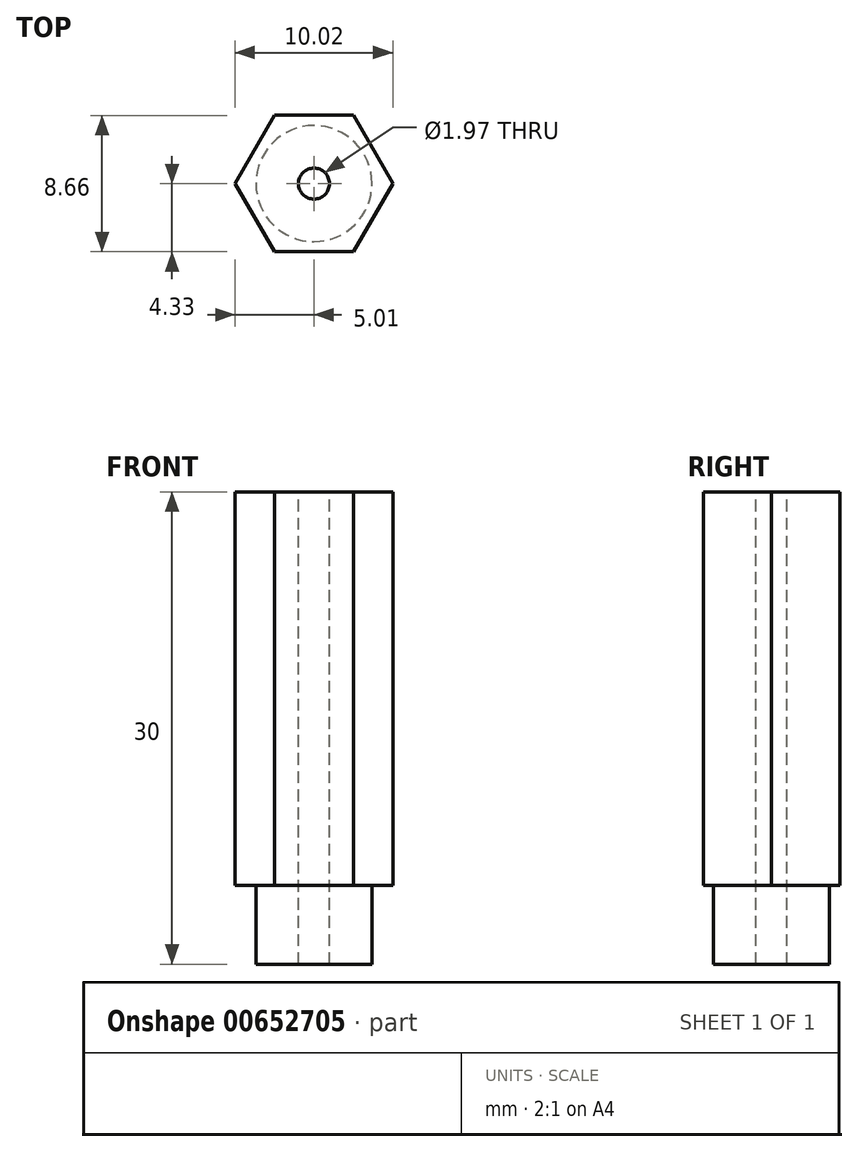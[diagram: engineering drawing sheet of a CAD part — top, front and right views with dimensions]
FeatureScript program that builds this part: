
annotation { "Feature Type Name" : "Feature", "Feature Type Description" : "" }
export const myFeature = defineFeature(function(context is Context, id is Id, definition is map)
    precondition{}
    {
        {
            var Q0;
            Q0=qCreatedBy(makeId("Top.planeOp"),FACE);
            var sketch = newSketch(context, id + "F0", { "sketchPlane" : qUnion([Q0])});
            skCircle(sketch, "E0.cCircle", {"center": v(0, 0) * mm, "radius": 4.33 * mm, "construction": true});
            skLineSegment(sketch, "E0.0", {"start": v(5, 0) * mm, "end": v(2.5, -4.33) * mm});
            skLineSegment(sketch, "E0.1", {"start": v(2.5, -4.33) * mm, "end": v(-2.5, -4.33) * mm});
            skLineSegment(sketch, "E0.2", {"start": v(-2.5, -4.33) * mm, "end": v(-5, 0) * mm});
            skLineSegment(sketch, "E0.3", {"start": v(-5, 0) * mm, "end": v(-2.5, 4.33) * mm});
            skLineSegment(sketch, "E0.4", {"start": v(-2.5, 4.33) * mm, "end": v(2.5, 4.33) * mm});
            skLineSegment(sketch, "E0.5", {"start": v(2.5, 4.33) * mm, "end": v(5, 0) * mm});
            skPoint(sketch, "E0.0.midPoint", {"position": v(3.75, -2.17) * mm});
            skCircle(sketch, "E1", {"center": v(0, 0) * mm, "radius": 3.69 * mm});
            skCircle(sketch, "E2", {"center": v(0, 0) * mm, "radius": 0.98 * mm});
            skSolve(sketch);
        }
        {
            var Q0;
            Q0=makeQuery(id+"F0.imprint","IMPRINT",FACE,{"disambiguationData":[TD([[makeQuery(id+"F0.imprint","IMPRINT",EDGE,{"derivedFrom":sQuery(id+"F0.wireOp",EDGE,"E1")}),1.0]])]});
            extrude(context, id + "F1", {"entities" : qUnion([Q0]), "oppositeDirection" : true, "depth" : 5 * mm, "offsetDistance" : 25 * mm});
        }
        {
            var Q0;
            Q0=qSketchRegion(id+"F0",true);
            var Q1;
            Q1=makeQuery(id+"F1.opExtrude","CAP_FACE",FACE,{"disambiguationData":[OSD([sQuery(id+"F0.wireOp",EDGE,"E1"),sQuery(id+"F0.wireOp",EDGE,"E2")])],"isStart":true});
            extrude(context, id + "F2", {"entities" : qUnion([Q0, Q1]), "operationType" : NewBodyOperationType.ADD, "depth" : 25 * mm, "offsetDistance" : 25 * mm});
        }
    });
